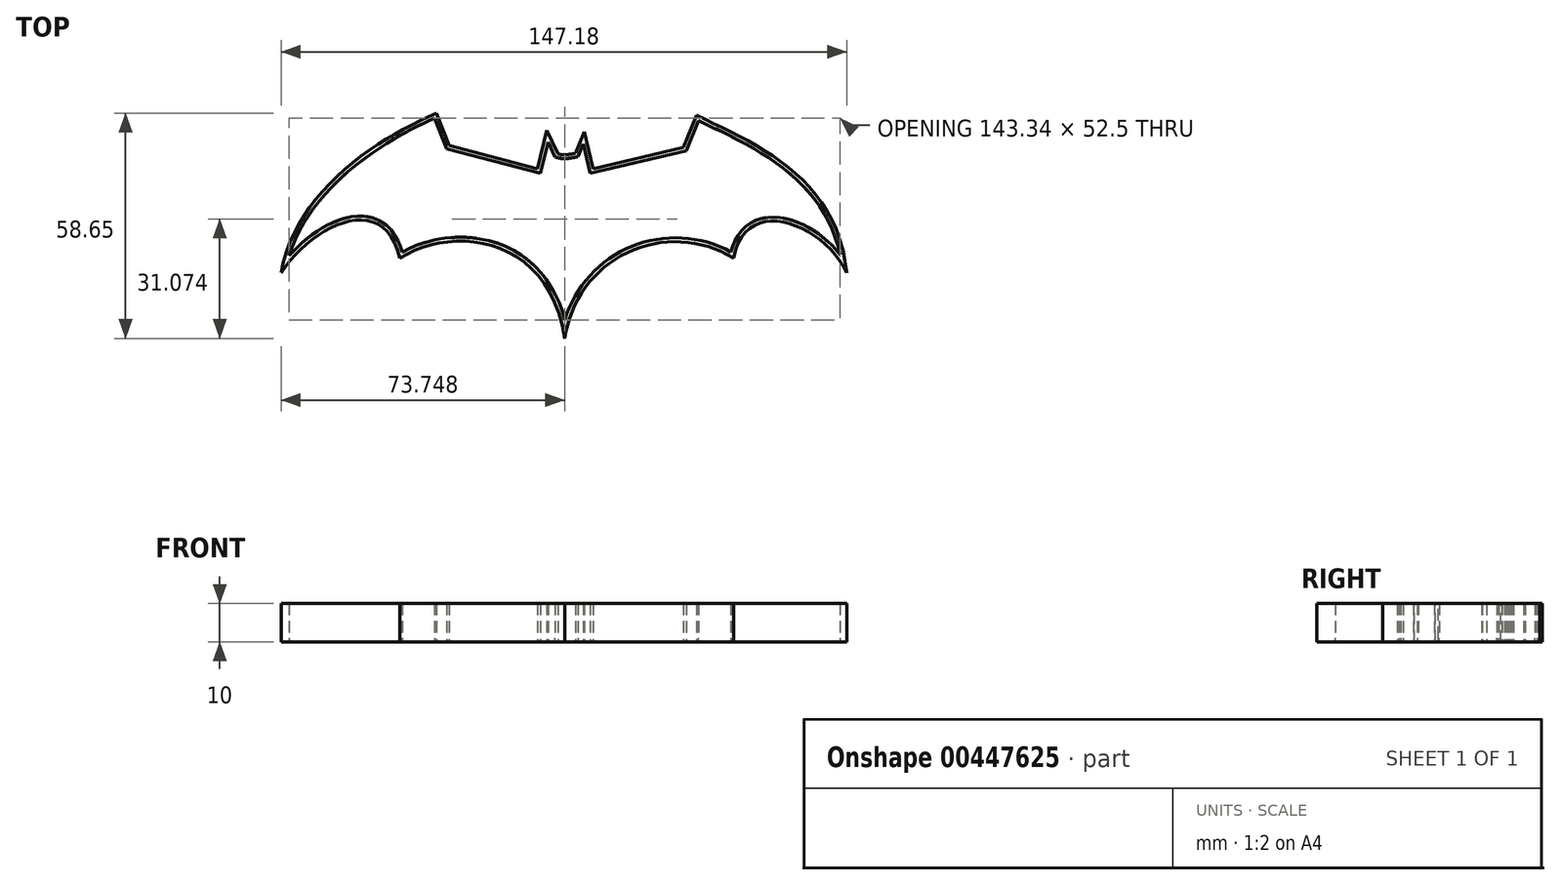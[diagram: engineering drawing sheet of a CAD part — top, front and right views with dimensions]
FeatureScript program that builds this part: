
annotation { "Feature Type Name" : "Feature", "Feature Type Description" : "" }
export const myFeature = defineFeature(function(context is Context, id is Id, definition is map)
    precondition{}
    {
        {
            var Q0;
            Q0=qCreatedBy(makeId("Top.planeOp"),FACE);
            var sketch = newSketch(context, id + "F0", { "sketchPlane" : qUnion([Q0])});
            skFitSpline(sketch, "E0", {"points": [v(-59.32, 0) * mm, v(-18.9, 41.52) * mm], "startDerivative": vector(10.6, 62.13) * mm, "endDerivative": vector(47.7, 20.02) * mm});
            skFitSpline(sketch, "E1", {"points": [v(-18.9, 41.52) * mm, v(-15.56, 33.08) * mm], "startDerivative": vector(3.34, -8.44) * mm, "endDerivative": vector(3.34, -8.44) * mm});
            skLineSegment(sketch, "E2", {"start": v(-15.56, 33.08) * mm, "end": v(7.4, 27.08) * mm});
            skLineSegment(sketch, "E3", {"start": v(9.83, 37.1) * mm, "end": v(7.4, 27.08) * mm});
            skPoint(sketch, "E4.startSnap0", {"position": v(8.62, 32.09) * mm});
            skFitSpline(sketch, "E5", {"points": [v(-28.42, 3.83) * mm, v(-59.32, 0) * mm], "startDerivative": vector(-12.7, 53.11) * mm, "endDerivative": vector(-24.37, -37.4) * mm});
            skFitSpline(sketch, "E6", {"points": [v(14.5, -17.13) * mm, v(-28.42, 3.83) * mm], "startDerivative": vector(-12.38, 81.7) * mm, "endDerivative": vector(-40.38, -25.48) * mm});
            skArc(sketch, "E7", {"start": v(58.4, 3.83) * mm, "mid": v(30.76, 5.25) * mm, "end": v(14.5, -17.13) * mm});
            skLineSegment(sketch, "E8", {"start": v(45.38, 32.65) * mm, "end": v(21.86, 27.08) * mm});
            skLineSegment(sketch, "E9", {"start": v(21.86, 27.08) * mm, "end": v(19.58, 36.71) * mm});
            skLineSegment(sketch, "E10", {"start": v(17.24, 31.1) * mm, "end": v(19.58, 36.71) * mm});
            skLineSegment(sketch, "E11", {"start": v(12.65, 30.96) * mm, "end": v(9.83, 37.1) * mm});
            skFitSpline(sketch, "E12", {"points": [v(12.65, 30.96) * mm, v(17.24, 31.1) * mm], "startDerivative": vector(4.54, -1.39) * mm, "endDerivative": vector(4.69, 1.06) * mm});
            skLineSegment(sketch, "E13", {"start": v(48.7, 40.97) * mm, "end": v(45.38, 32.65) * mm});
            skFitSpline(sketch, "E14", {"points": [v(58.4, 3.83) * mm, v(87.86, 0) * mm], "startDerivative": vector(9.88, 51.23) * mm, "endDerivative": vector(17.76, -37.48) * mm});
            skFitSpline(sketch, "E15", {"points": [v(48.7, 40.97) * mm, v(87.86, 0) * mm], "startDerivative": vector(50.15, -23.74) * mm, "endDerivative": vector(7.48, -73) * mm});
            skSolve(sketch);
        }
        {
            var Q0;
            Q0 = qSketchRegion(id + "F0", true);
            extrude(context, id + "F1", {"entities" : qUnion([Q0]), "depth" : 10 * mm});
        }
        {
            var Q0;
            Q0=makeQuery(id+"F1.opExtrude","CAP_FACE",FACE,{"disambiguationData":[OSD([sQuery(id+"F0.wireOp",EDGE,"E0"),sQuery(id+"F0.wireOp",EDGE,"E1"),sQuery(id+"F0.wireOp",EDGE,"E2"),sQuery(id+"F0.wireOp",EDGE,"E3"),sQuery(id+"F0.wireOp",EDGE,"E5"),sQuery(id+"F0.wireOp",EDGE,"E6"),sQuery(id+"F0.wireOp",EDGE,"E7"),sQuery(id+"F0.wireOp",EDGE,"E8"),sQuery(id+"F0.wireOp",EDGE,"E9"),sQuery(id+"F0.wireOp",EDGE,"E10"),sQuery(id+"F0.wireOp",EDGE,"E11"),sQuery(id+"F0.wireOp",EDGE,"E12"),sQuery(id+"F0.wireOp",EDGE,"E13"),sQuery(id+"F0.wireOp",EDGE,"E14"),sQuery(id+"F0.wireOp",EDGE,"E15")])],"isStart":false});
            shell(context, id + "F2", {"entities" : qUnion([Q0]), "thickness" : 1 * mm});
        }
        {
            var Q0;
            Q0=makeQuery(id+"F2.opShell","OFFSET_FACE",FACE,{"disambiguationData":[OSD([sQuery(id+"F0.wireOp",EDGE,"E0"),sQuery(id+"F0.wireOp",EDGE,"E1"),sQuery(id+"F0.wireOp",EDGE,"E2"),sQuery(id+"F0.wireOp",EDGE,"E3"),sQuery(id+"F0.wireOp",EDGE,"E5"),sQuery(id+"F0.wireOp",EDGE,"E6"),sQuery(id+"F0.wireOp",EDGE,"E7"),sQuery(id+"F0.wireOp",EDGE,"E8"),sQuery(id+"F0.wireOp",EDGE,"E9"),sQuery(id+"F0.wireOp",EDGE,"E10"),sQuery(id+"F0.wireOp",EDGE,"E11"),sQuery(id+"F0.wireOp",EDGE,"E12"),sQuery(id+"F0.wireOp",EDGE,"E13"),sQuery(id+"F0.wireOp",EDGE,"E14"),sQuery(id+"F0.wireOp",EDGE,"E15")])]});
            var sketch = newSketch(context, id + "F3", { "sketchPlane" : qUnion([Q0])});
            skCircle(sketch, "E16", {"center": v(-23.85, 22.2) * mm, "radius": 10.88 * mm});
            skCircle(sketch, "E17", {"center": v(14.48, 12) * mm, "radius": 11.38 * mm});
            skCircle(sketch, "E18", {"center": v(51.57, 20.47) * mm, "radius": 10.34 * mm});
            skSolve(sketch);
        }
        {
            var Q0;
            Q0=makeQuery(id+"F1.opExtrude","CAP_FACE",FACE,{"disambiguationData":[OSD([sQuery(id+"F0.wireOp",EDGE,"E0"),sQuery(id+"F0.wireOp",EDGE,"E1"),sQuery(id+"F0.wireOp",EDGE,"E2"),sQuery(id+"F0.wireOp",EDGE,"E3"),sQuery(id+"F0.wireOp",EDGE,"E5"),sQuery(id+"F0.wireOp",EDGE,"E6"),sQuery(id+"F0.wireOp",EDGE,"E7"),sQuery(id+"F0.wireOp",EDGE,"E8"),sQuery(id+"F0.wireOp",EDGE,"E9"),sQuery(id+"F0.wireOp",EDGE,"E10"),sQuery(id+"F0.wireOp",EDGE,"E11"),sQuery(id+"F0.wireOp",EDGE,"E12"),sQuery(id+"F0.wireOp",EDGE,"E13"),sQuery(id+"F0.wireOp",EDGE,"E14"),sQuery(id+"F0.wireOp",EDGE,"E15")])],"isStart":true});
            var Q1;
            Q1=makeQuery(id+"F2.opShell","OFFSET_FACE",FACE,{"disambiguationData":[OSD([sQuery(id+"F0.wireOp",EDGE,"E0"),sQuery(id+"F0.wireOp",EDGE,"E1"),sQuery(id+"F0.wireOp",EDGE,"E2"),sQuery(id+"F0.wireOp",EDGE,"E3"),sQuery(id+"F0.wireOp",EDGE,"E5"),sQuery(id+"F0.wireOp",EDGE,"E6"),sQuery(id+"F0.wireOp",EDGE,"E7"),sQuery(id+"F0.wireOp",EDGE,"E8"),sQuery(id+"F0.wireOp",EDGE,"E9"),sQuery(id+"F0.wireOp",EDGE,"E10"),sQuery(id+"F0.wireOp",EDGE,"E11"),sQuery(id+"F0.wireOp",EDGE,"E12"),sQuery(id+"F0.wireOp",EDGE,"E13"),sQuery(id+"F0.wireOp",EDGE,"E14"),sQuery(id+"F0.wireOp",EDGE,"E15")])]});
            var Q2;
            Q2 = qSketchRegion(id + "F3", true);
            extrude(context, id + "F4", {"entities" : qUnion([Q0, Q1, Q2]), "operationType" : NewBodyOperationType.REMOVE, "depth" : 25 * mm});
        }
    });
